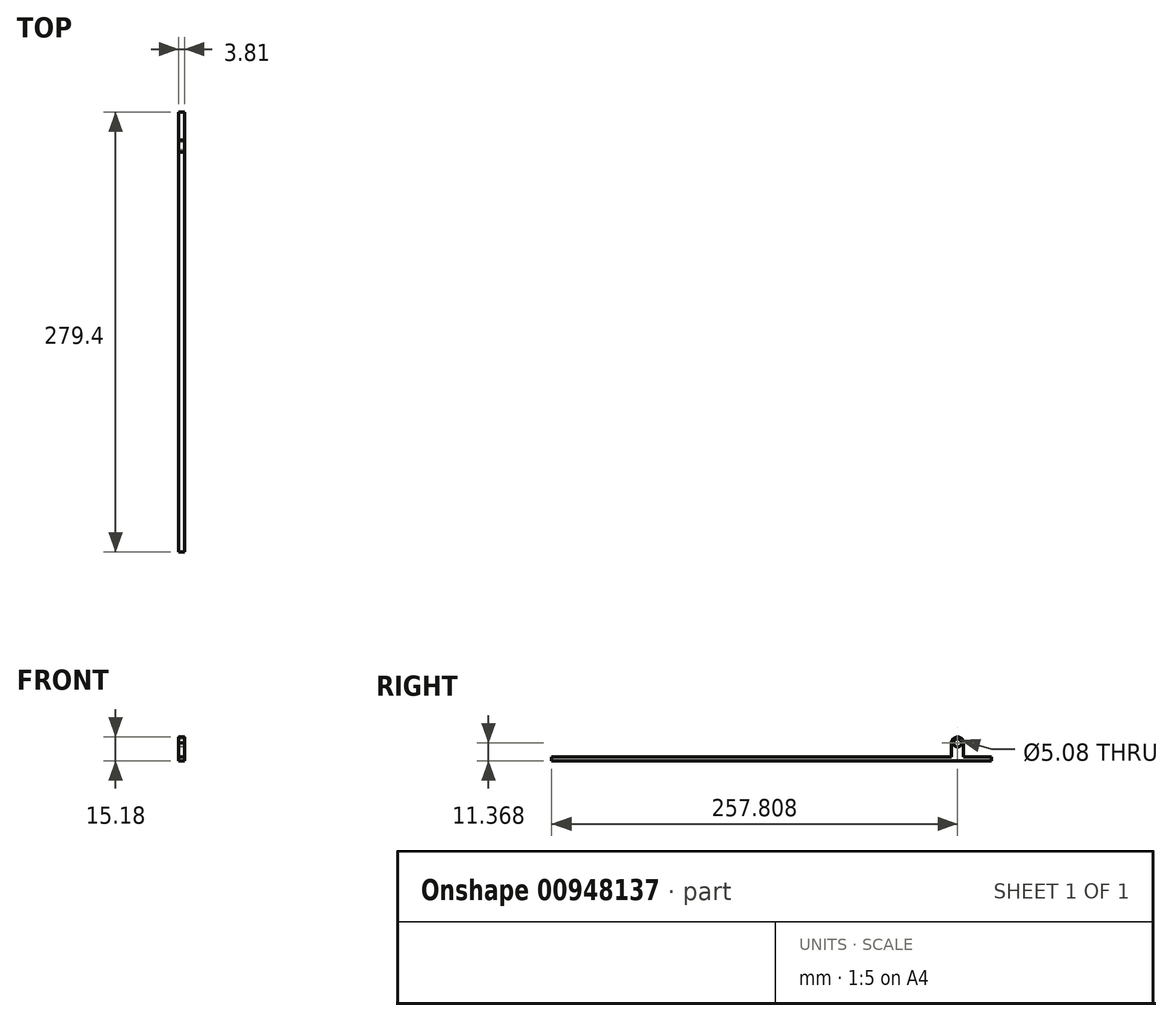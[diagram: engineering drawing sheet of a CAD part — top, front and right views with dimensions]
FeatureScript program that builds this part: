
annotation { "Feature Type Name" : "Feature", "Feature Type Description" : "" }
export const myFeature = defineFeature(function(context is Context, id is Id, definition is map)
    precondition{}
    {
        {
            var Q0;
            Q0=qCreatedBy(makeId("Right.planeOp"),FACE);
            var sketch = newSketch(context, id + "F0", { "sketchPlane" : qUnion([Q0])});
            skLineSegment(sketch, "E0.bottom", {"start": v(-18.73, 19) * mm, "end": v(-11.11, 19) * mm});
            skLineSegment(sketch, "E0.top", {"start": v(-18.73, 11.38) * mm, "end": v(-11.11, 11.38) * mm});
            skLineSegment(sketch, "E0.left", {"start": v(-18.73, 19) * mm, "end": v(-18.73, 11.38) * mm});
            skLineSegment(sketch, "E0.right", {"start": v(-11.11, 19) * mm, "end": v(-11.11, 11.38) * mm});
            skArc(sketch, "E1", {"start": v(-11.11, 15.2) * mm, "mid": v(-14.92, 18.94) * mm, "end": v(-18.73, 15.2) * mm});
            skCircle(sketch, "E2", {"center": v(-14.92, 15.13) * mm, "radius": 2.54 * mm});
            skSolve(sketch);
        }
        {
            var Q0;
            {var subQ1=sQuery(id+"F0.wireOp",EDGE,"E0.top");Q0=makeQuery(id+"F0.imprint","IMPRINT",FACE,{"disambiguationData":[TD([[makeQuery(id+"F0.imprint","IMPRINT",EDGE,{"derivedFrom":subQ1}),1.0]])]});}
            extrude(context, id + "F1", {"entities" : qUnion([Q0]), "depth" : 3.8 * mm, "offsetDistance" : 25.4 * mm});
        }
        {
            var Q0;
            Q0=makeQuery(id+"F1.opExtrude","SWEPT_FACE",FACE,{"disambiguationData":[OSD([sQuery(id+"F0.wireOp",EDGE,"E0.top")])]});
            extrude(context, id + "F2", {"entities" : qUnion([Q0]), "operationType" : NewBodyOperationType.ADD, "depth" : 7.62 * mm, "offsetDistance" : 25.4 * mm});
        }
        {
            var Q0;
            {var subQ0=sQuery(id+"F0.wireOp",EDGE,"E0.left");Q0=makeQuery(id+"F2.boolean.opBoolean","MERGE",FACE,{"derivedFrom":[makeQuery(id+"F1.opExtrude","SWEPT_FACE",FACE,{"disambiguationData":[OSD([subQ0])]}),makeQuery(id+"F2.opExtrude","SWEPT_FACE",FACE,{"disambiguationData":[OSD([sQuery(id+"F0.wireOp",EDGE,"E0.top"),subQ0])]})]});}
            var sketch = newSketch(context, id + "F3", { "sketchPlane" : qUnion([Q0])});
            skLineSegment(sketch, "E3.bottom", {"start": v(0, 3.76) * mm, "end": v(3.81, 3.76) * mm});
            skLineSegment(sketch, "E3.top", {"start": v(0, 6.3) * mm, "end": v(3.81, 6.3) * mm});
            skLineSegment(sketch, "E3.left", {"start": v(0, 3.76) * mm, "end": v(0, 6.3) * mm});
            skLineSegment(sketch, "E3.right", {"start": v(3.81, 3.76) * mm, "end": v(3.81, 6.3) * mm});
            skSolve(sketch);
        }
        {
            var Q0;
            Q0=makeQuery(id+"F3.imprint","IMPRINT",FACE,{"disambiguationData":[TD([[makeQuery(id+"F3.imprint","IMPRINT",EDGE,{"derivedFrom":sQuery(id+"F3.wireOp",EDGE,"E3.bottom")}),-1.0]])]});
            extrude(context, id + "F4", {"entities" : qUnion([Q0]), "operationType" : NewBodyOperationType.ADD, "depth" : 254 * mm, "offsetDistance" : 25.4 * mm, "hasSecondDirection" : true, "secondDirectionOppositeDirection" : true, "secondDirectionDepth" : 25.4 * mm});
        }
    });
